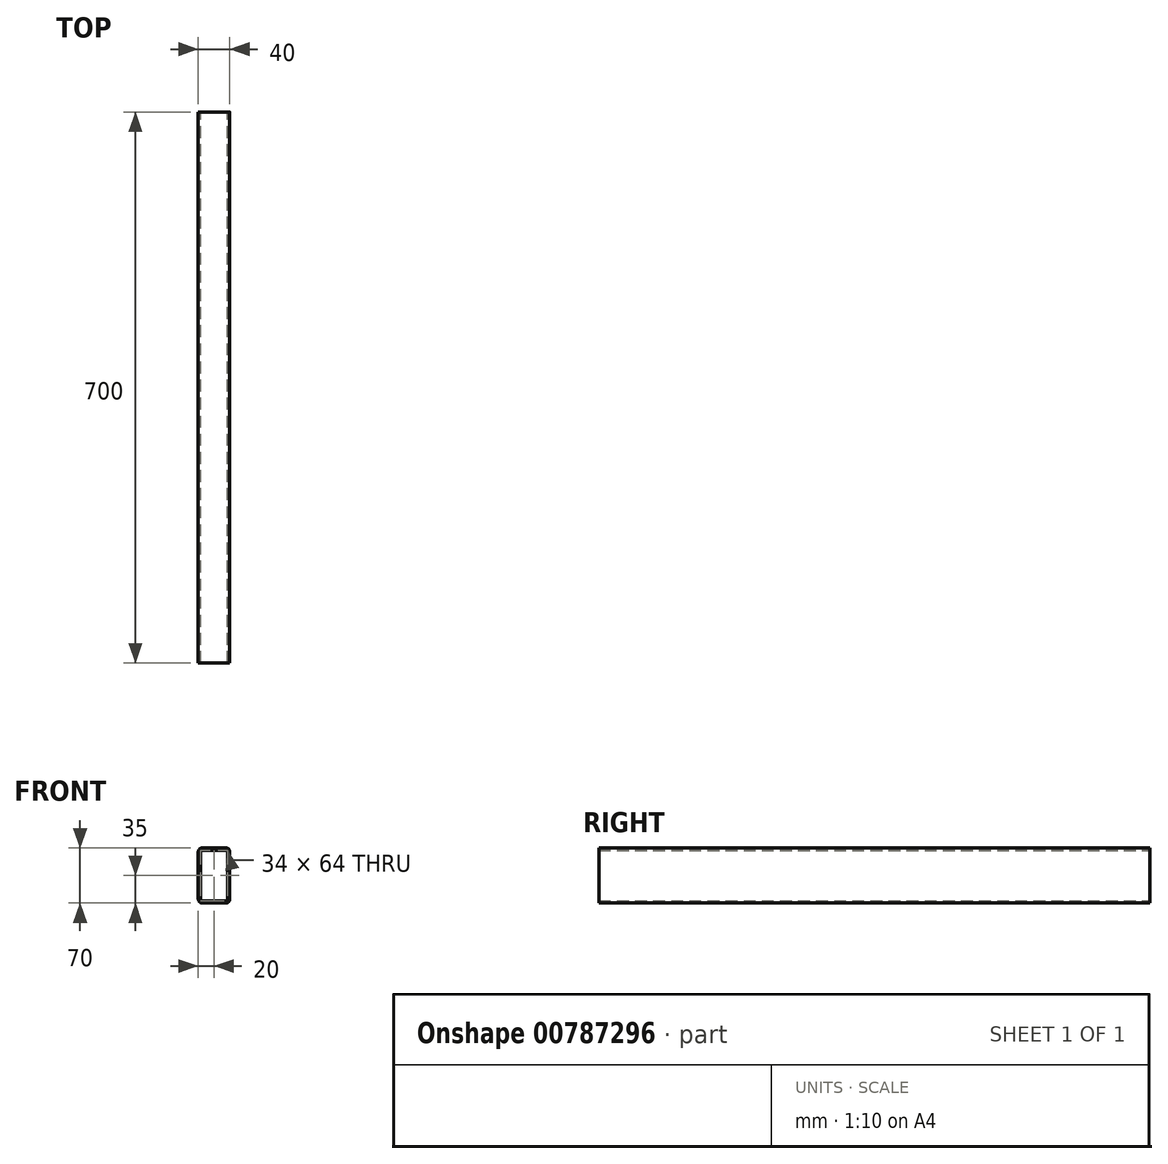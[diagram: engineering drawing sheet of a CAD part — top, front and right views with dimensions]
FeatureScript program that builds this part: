
annotation { "Feature Type Name" : "Feature", "Feature Type Description" : "" }
export const myFeature = defineFeature(function(context is Context, id is Id, definition is map)
    precondition{}
    {
        {
            var Q0;
            Q0=qCreatedBy(makeId("Front.planeOp"),FACE);
            var sketch = newSketch(context, id + "F0", { "sketchPlane" : qUnion([Q0])});
            skLineSegment(sketch, "E0.bottom", {"start": v(15, 35) * mm, "end": v(-15, 35) * mm});
            skLineSegment(sketch, "E0.top", {"start": v(15, -35) * mm, "end": v(-15, -35) * mm});
            skLineSegment(sketch, "E0.left", {"start": v(20, 30) * mm, "end": v(20, -30) * mm});
            skLineSegment(sketch, "E0.right", {"start": v(-20, 30) * mm, "end": v(-20, -30) * mm});
            skPoint(sketch, "E0.middle", {"position": v(0, 0) * mm});
            skPoint(sketch, "E1.visualSharp", {"position": v(-20, 35) * mm});
            skArc(sketch, "E1.filletArc", {"start": v(-15, 35) * mm, "mid": v(-18.54, 33.54) * mm, "end": v(-20, 30) * mm});
            skPoint(sketch, "E2.visualSharp", {"position": v(20, 35) * mm});
            skArc(sketch, "E2.filletArc", {"start": v(20, 30) * mm, "mid": v(18.54, 33.54) * mm, "end": v(15, 35) * mm});
            skPoint(sketch, "E3.visualSharp", {"position": v(20, -35) * mm});
            skArc(sketch, "E3.filletArc", {"start": v(15, -35) * mm, "mid": v(18.54, -33.54) * mm, "end": v(20, -30) * mm});
            skPoint(sketch, "E4.visualSharp", {"position": v(-20, -35) * mm});
            skArc(sketch, "E4.filletArc", {"start": v(-20, -30) * mm, "mid": v(-18.54, -33.54) * mm, "end": v(-15, -35) * mm});
            skLineSegment(sketch, "E5.0", {"start": v(-17, 32) * mm, "end": v(-17, -32) * mm});
            skLineSegment(sketch, "E5.1", {"start": v(17, 32) * mm, "end": v(-17, 32) * mm});
            skLineSegment(sketch, "E5.2", {"start": v(17, 32) * mm, "end": v(17, -32) * mm});
            skLineSegment(sketch, "E5.3", {"start": v(17, -32) * mm, "end": v(-17, -32) * mm});
            skSolve(sketch);
        }
        {
            var Q0;
            Q0=makeQuery(id+"F0.imprint","IMPRINT",FACE,{"disambiguationData":[TD([[makeQuery(id+"F0.imprint","IMPRINT",EDGE,{"derivedFrom":sQuery(id+"F0.wireOp",EDGE,"E0.bottom")}),1.0]])]});
            extrude(context, id + "F1", {"entities" : qUnion([Q0]), "depth" : 700 * mm, "offsetDistance" : 25 * mm});
        }
    });
